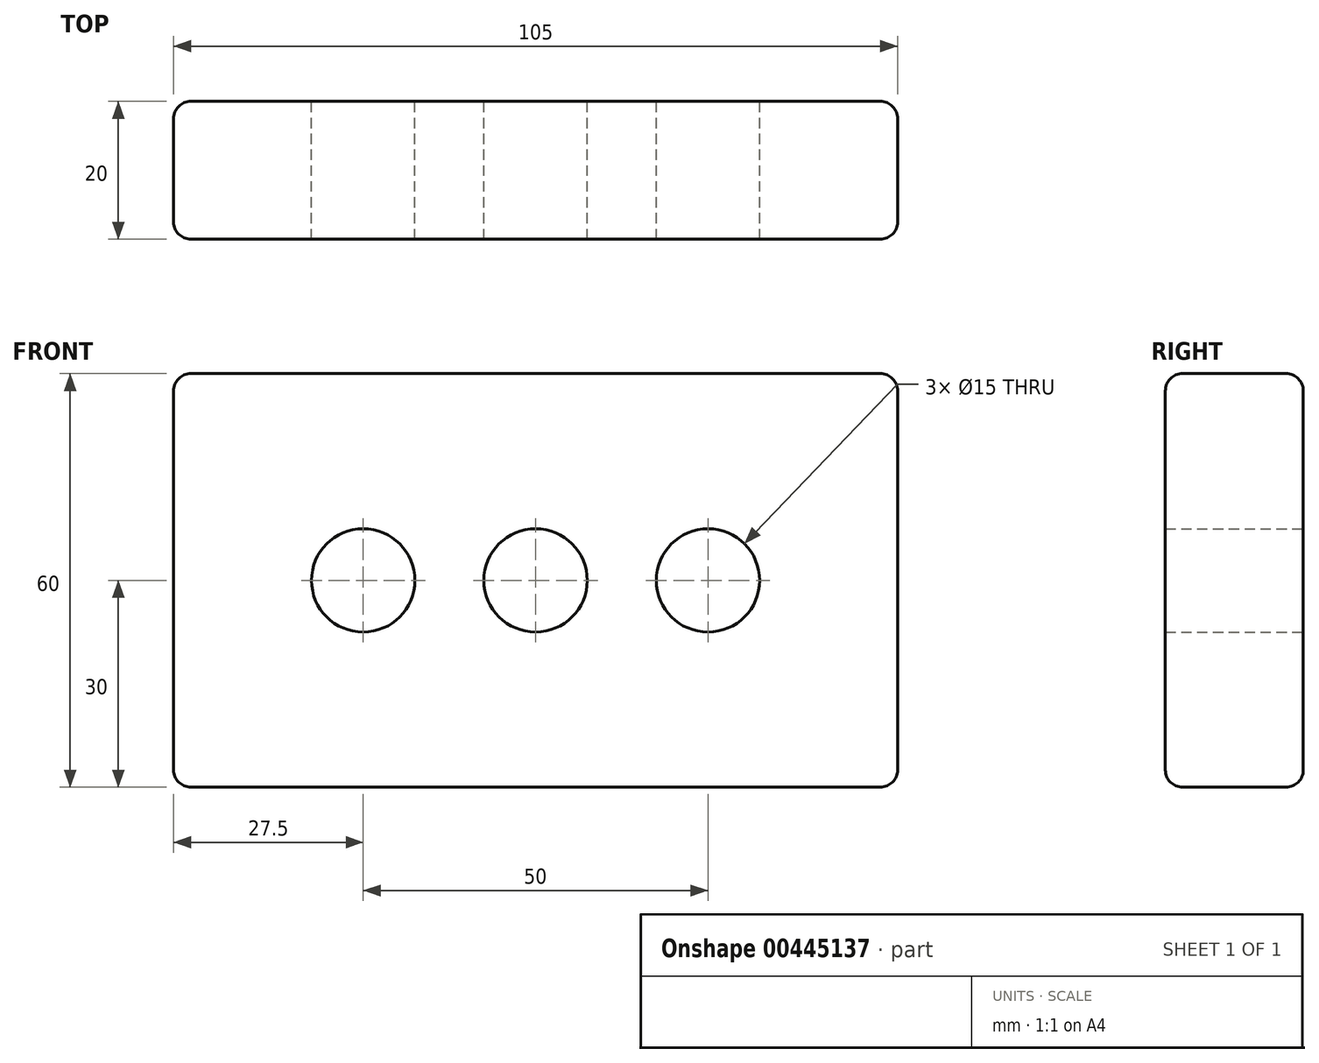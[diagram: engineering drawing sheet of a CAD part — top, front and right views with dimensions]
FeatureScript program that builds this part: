
annotation { "Feature Type Name" : "Feature", "Feature Type Description" : "" }
export const myFeature = defineFeature(function(context is Context, id is Id, definition is map)
    precondition{}
    {
        {
            var Q0;
            Q0=qCreatedBy(makeId("Front.planeOp"),FACE);
            var sketch = newSketch(context, id + "F0", { "sketchPlane" : qUnion([Q0])});
            skLineSegment(sketch, "E0.bottom", {"start": v(52.5, 30) * mm, "end": v(-52.5, 30) * mm});
            skLineSegment(sketch, "E0.top", {"start": v(52.5, -30) * mm, "end": v(-52.5, -30) * mm});
            skLineSegment(sketch, "E0.left", {"start": v(52.5, 30) * mm, "end": v(52.5, -30) * mm});
            skLineSegment(sketch, "E0.right", {"start": v(-52.5, 30) * mm, "end": v(-52.5, -30) * mm});
            skPoint(sketch, "E0.middle", {"position": v(0, 0) * mm});
            skCircle(sketch, "E1", {"center": v(0, 0) * mm, "radius": 7.5 * mm});
            skCircle(sketch, "E2", {"center": v(-25, 0) * mm, "radius": 7.5 * mm});
            skCircle(sketch, "E3", {"center": v(25, 0) * mm, "radius": 7.5 * mm});
            skLineSegment(sketch, "E4", {"start": v(-17.5, 0) * mm, "end": v(-7.5, 0) * mm});
            skLineSegment(sketch, "E5", {"start": v(7.5, 0) * mm, "end": v(17.5, 0) * mm});
            skSolve(sketch);
        }
        {
            var Q0;
            Q0 = qSketchRegion(id + "F0", true);
            extrude(context, id + "F1", {"entities" : qUnion([Q0]), "depth" : 20 * mm});
        }
        {
            var Q0;
            Q0=makeQuery(id+"F1.opExtrude","CAP_EDGE",EDGE,{"disambiguationData":[OSD([sQuery(id+"F0.wireOp",EDGE,"E0.top")])],"isStart":false});
            var Q1;
            Q1=makeQuery(id+"F1.opExtrude","CAP_EDGE",EDGE,{"disambiguationData":[OSD([sQuery(id+"F0.wireOp",EDGE,"E0.left")])],"isStart":false});
            var Q2;
            Q2=makeQuery(id+"F1.opExtrude","CAP_EDGE",EDGE,{"disambiguationData":[OSD([sQuery(id+"F0.wireOp",EDGE,"E0.bottom")])],"isStart":false});
            var Q3;
            Q3=makeQuery(id+"F1.opExtrude","CAP_EDGE",EDGE,{"disambiguationData":[OSD([sQuery(id+"F0.wireOp",EDGE,"E0.right")])],"isStart":false});
            var Q4;
            Q4=makeQuery(id+"F1.opExtrude","CAP_EDGE",EDGE,{"disambiguationData":[OSD([sQuery(id+"F0.wireOp",EDGE,"E0.top")])],"isStart":true});
            var Q5;
            Q5=makeQuery(id+"F1.opExtrude","SWEPT_EDGE",EDGE,{"disambiguationData":[OSD([sQuery(id+"F0.wireOp",EDGE,"E0.top"),sQuery(id+"F0.wireOp",EDGE,"E0.left")])]});
            var Q6;
            Q6=makeQuery(id+"F1.opExtrude","CAP_EDGE",EDGE,{"disambiguationData":[OSD([sQuery(id+"F0.wireOp",EDGE,"E0.left")])],"isStart":true});
            var Q7;
            Q7=makeQuery(id+"F1.opExtrude","SWEPT_EDGE",EDGE,{"disambiguationData":[OSD([sQuery(id+"F0.wireOp",EDGE,"E0.top"),sQuery(id+"F0.wireOp",EDGE,"E0.right")])]});
            var Q8;
            Q8=makeQuery(id+"F1.opExtrude","SWEPT_FACE",FACE,{"disambiguationData":[OSD([sQuery(id+"F0.wireOp",EDGE,"E0.right")])]});
            var Q9;
            Q9=makeQuery(id+"F1.opExtrude","SWEPT_EDGE",EDGE,{"disambiguationData":[OSD([sQuery(id+"F0.wireOp",EDGE,"E0.bottom"),sQuery(id+"F0.wireOp",EDGE,"E0.left")])]});
            var Q10;
            Q10=makeQuery(id+"F1.opExtrude","CAP_EDGE",EDGE,{"disambiguationData":[OSD([sQuery(id+"F0.wireOp",EDGE,"E0.bottom")])],"isStart":true});
            fillet(context, id + "F2", {"entities" : qUnion([Q0, Q1, Q2, Q3, Q4, Q5, Q6, Q7, Q8, Q9, Q10]), "radius" : 2.5 * mm, "tangentPropagation" : true, "allowEdgeOverflow" : false});
        }
    });
